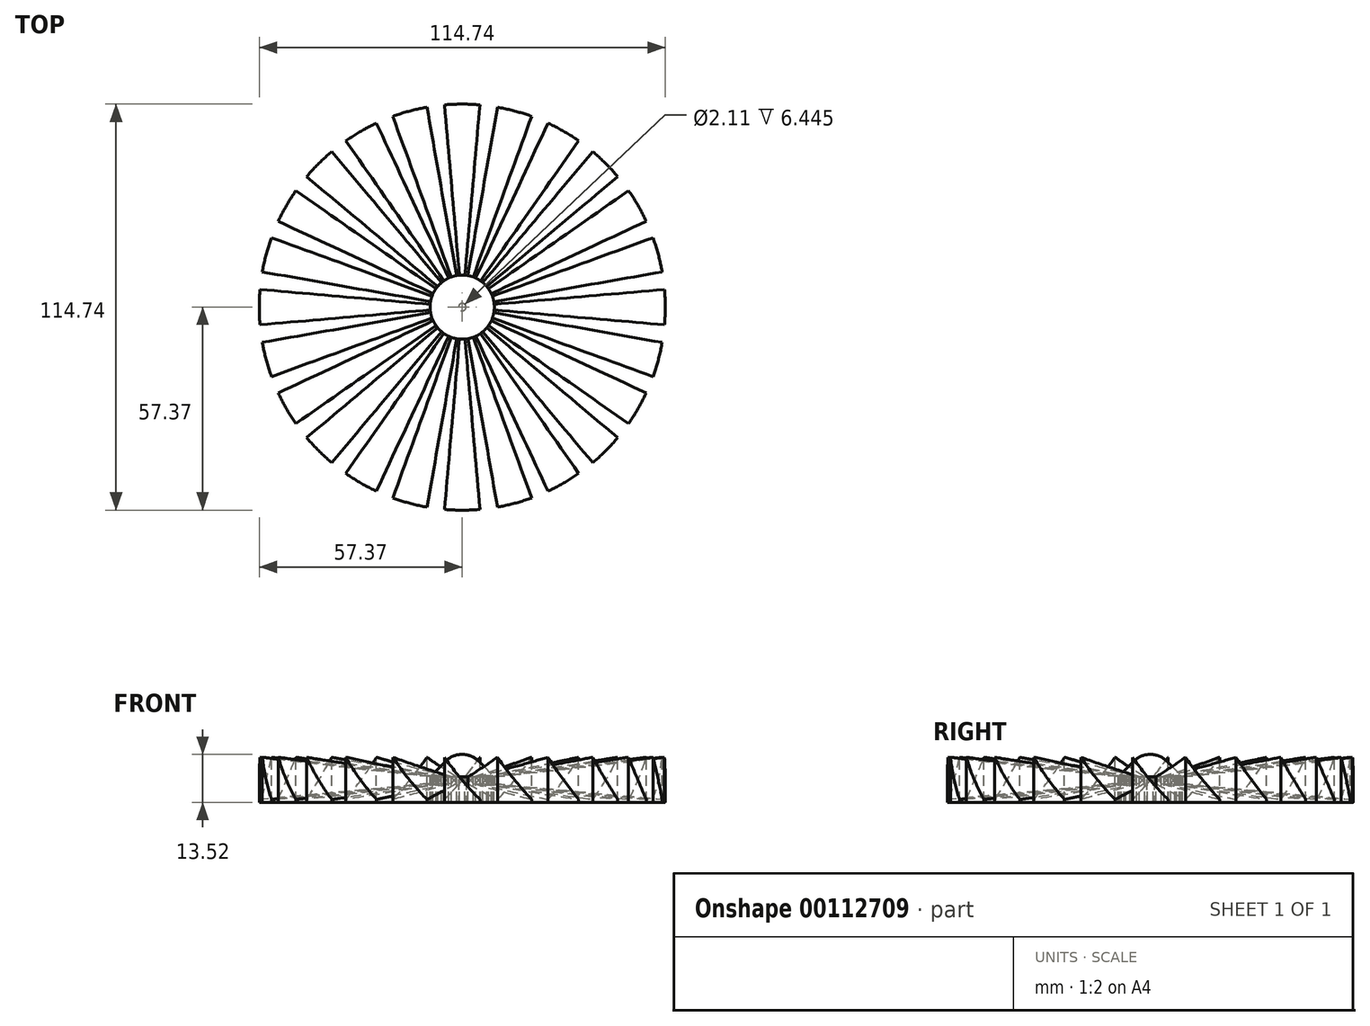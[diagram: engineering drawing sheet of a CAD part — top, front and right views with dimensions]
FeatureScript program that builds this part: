
annotation { "Feature Type Name" : "Feature", "Feature Type Description" : "" }
export const myFeature = defineFeature(function(context is Context, id is Id, definition is map)
    precondition{}
    {
        {
            var Q0;
            Q0=qCreatedBy(makeId("Top.planeOp"),FACE);
            var sketch = newSketch(context, id + "F0", { "sketchPlane" : qUnion([Q0])});
            skLineSegment(sketch, "E0", {"start": v(-5, -57.15) * mm, "end": v(5, -57.15) * mm, "construction": true});
            skLineSegment(sketch, "E1", {"start": v(0, 0) * mm, "end": v(0, -57.15) * mm, "construction": true});
            skArc(sketch, "E2", {"start": v(-5, -57.15) * mm, "mid": v(0, -57.37) * mm, "end": v(5, -57.15) * mm});
            skLineSegment(sketch, "E3", {"start": v(5, -57.15) * mm, "end": v(0.8, -9.07) * mm});
            skLineSegment(sketch, "E4", {"start": v(-5, -57.15) * mm, "end": v(-0.8, -9.07) * mm});
            skLineSegment(sketch, "E5", {"start": v(0, 0) * mm, "end": v(-0.8, -9.07) * mm});
            skLineSegment(sketch, "E6", {"start": v(0, 0) * mm, "end": v(0.8, -9.07) * mm});
            skLineSegment(sketch, "E7", {"start": v(0.8, -9.07) * mm, "end": v(-0.8, -9.07) * mm, "construction": true});
            skCircle(sketch, "E8", {"center": v(0, 0) * mm, "radius": 9.07 * mm, "construction": true});
            skSolve(sketch);
        }
        {
            var Q0;
            Q0=qSketchRegion(id+"F0",true);
            extrude(context, id + "F1", {"entities" : qUnion([Q0]), "depth" : 12.7 * mm});
        }
        {
            var Q0;
            Q0=qCreatedBy(makeId("Front.planeOp"),FACE);
            var sketch = newSketch(context, id + "F2", { "sketchPlane" : qUnion([Q0])});
            skLineSegment(sketch, "E9.bottom", {"start": v(5, 0) * mm, "end": v(-5, 0) * mm, "construction": true});
            skLineSegment(sketch, "E9.top", {"start": v(5, 12.7) * mm, "end": v(-5, 12.7) * mm});
            skLineSegment(sketch, "E9.left", {"start": v(-5, 0) * mm, "end": v(-5, 12.7) * mm, "construction": true});
            skLineSegment(sketch, "E9.right", {"start": v(5, 0.8) * mm, "end": v(5, 12.7) * mm});
            skLineSegment(sketch, "E10", {"start": v(5, 0) * mm, "end": v(5, 0.8) * mm});
            skArc(sketch, "E11", {"start": v(-5, 12.7) * mm, "mid": v(-0.26, 6.53) * mm, "end": v(5, 0.8) * mm});
            skLineSegment(sketch, "E12", {"start": v(5, 0.8) * mm, "end": v(11.73, -5.93) * mm, "construction": true});
            skSolve(sketch);
        }
        {
            var Q0;
            Q0=qSketchRegion(id+"F2",true);
            var Q1;
            Q1=makeQuery(id+"F1.opExtrude","SWEPT_FACE",FACE,{"disambiguationData":[OSD([sQuery(id+"F0.wireOp",EDGE,"E2")])]});
            extrude(context, id + "F3", {"entities" : qUnion([Q0]), "operationType" : NewBodyOperationType.REMOVE, "endBound" : BoundingType.UP_TO_SURFACE, "endBoundEntityFace" : qUnion([Q1]), "depth" : 25.4 * mm});
        }
        {
            var Q0;
            Q0=makeQuery(id+"F1.opExtrude","CAP_FACE",FACE,{"disambiguationData":[OSD([sQuery(id+"F0.wireOp",EDGE,"E2"),sQuery(id+"F0.wireOp",EDGE,"E3"),sQuery(id+"F0.wireOp",EDGE,"E4"),sQuery(id+"F0.wireOp",EDGE,"E5"),sQuery(id+"F0.wireOp",EDGE,"E6")])],"isStart":true});
            var sketch = newSketch(context, id + "F4", { "sketchPlane" : qUnion([Q0])});
            skLineSegment(sketch, "E13", {"start": v(-5, 57.15) * mm, "end": v(-5, 57.15) * mm});
            skLineSegment(sketch, "E14", {"start": v(-5, 57.15) * mm, "end": v(0, 0) * mm});
            skLineSegment(sketch, "E15", {"start": v(0, 0) * mm, "end": v(5, 57.15) * mm});
            skLineSegment(sketch, "E16", {"start": v(5, 57.15) * mm, "end": v(5, 57.15) * mm});
            skArc(sketch, "E17", {"start": v(5, 57.15) * mm, "mid": v(0, 57.37) * mm, "end": v(-5, 57.15) * mm, "construction": true});
            skArc(sketch, "E18", {"start": v(-5, 57.15) * mm, "mid": v(0, -57.37) * mm, "end": v(5, 57.15) * mm});
            skSolve(sketch);
        }
        {
            var Q0;
            Q0=qSketchRegion(id+"F4",true);
            extrude(context, id + "F5", {"entities" : qUnion([Q0]), "operationType" : NewBodyOperationType.ADD, "oppositeDirection" : true, "depth" : 12.7 * mm});
        }
        {
            var Q0;
            Q0=makeQuery(id+"F5.opExtrude","CAP_FACE",FACE,{"disambiguationData":[OSD([sQuery(id+"F4.wireOp",EDGE,"E13"),sQuery(id+"F4.wireOp",EDGE,"E14"),sQuery(id+"F4.wireOp",EDGE,"E15"),sQuery(id+"F4.wireOp",EDGE,"E16"),sQuery(id+"F4.wireOp",EDGE,"E18")])],"isStart":false});
            var sketch = newSketch(context, id + "F6", { "sketchPlane" : qUnion([Q0])});
            skCircle(sketch, "E19", {"center": v(0, 0) * mm, "radius": 9.07 * mm});
            skSolve(sketch);
        }
        {
            var Q0;
            Q0=qSketchRegion(id+"F6",true);
            var Q1;
            Q1=makeQuery(id+"F5.boolean.opBoolean","MERGE",FACE,{"derivedFrom":[makeQuery(id+"F1.opExtrude","CAP_FACE",FACE,{"disambiguationData":[OSD([sQuery(id+"F0.wireOp",EDGE,"E2"),sQuery(id+"F0.wireOp",EDGE,"E3"),sQuery(id+"F0.wireOp",EDGE,"E4"),sQuery(id+"F0.wireOp",EDGE,"E5"),sQuery(id+"F0.wireOp",EDGE,"E6")])],"isStart":true}),makeQuery(id+"F5.opExtrude","CAP_FACE",FACE,{"disambiguationData":[OSD([sQuery(id+"F4.wireOp",EDGE,"E13"),sQuery(id+"F4.wireOp",EDGE,"E14"),sQuery(id+"F4.wireOp",EDGE,"E15"),sQuery(id+"F4.wireOp",EDGE,"E16"),sQuery(id+"F4.wireOp",EDGE,"E18")])],"isStart":true})]});
            extrude(context, id + "F7", {"entities" : qUnion([Q0]), "operationType" : NewBodyOperationType.ADD, "endBound" : BoundingType.UP_TO_SURFACE, "oppositeDirection" : true, "endBoundEntityFace" : qUnion([Q1]), "depth" : 25.4 * mm});
        }
        {
            var Q0;
            Q0=makeQuery(id+"F7.opExtrude","SWEPT_FACE",FACE,{"disambiguationData":[OSD([sQuery(id+"F6.wireOp",EDGE,"E19")])]});
            var Q1;
            Q1=makeQuery(id+"F3.boolean.opBoolean","COPY",FACE,{"derivedFrom":makeQuery(id+"F3.opExtrude","SWEPT_FACE",FACE,{"disambiguationData":[OSD([sQuery(id+"F2.wireOp",EDGE,"E11")])]})});
            var Q2;
            Q2=makeQuery(id+"F5.opExtrude","SWEPT_FACE",FACE,{"disambiguationData":[OSD([sQuery(id+"F4.wireOp",EDGE,"E15")])]});
            var Q3;
            Q3=makeQuery(id+"F5.opExtrude","SWEPT_FACE",FACE,{"disambiguationData":[OSD([sQuery(id+"F4.wireOp",EDGE,"E14")])]});
            var Q4;
            Q4=makeQuery(id+"F5.boolean.opBoolean","MERGE",FACE,{"derivedFrom":[makeQuery(id+"F1.opExtrude","SWEPT_FACE",FACE,{"disambiguationData":[OSD([sQuery(id+"F0.wireOp",EDGE,"E2")])]}),makeQuery(id+"F5.opExtrude","SWEPT_FACE",FACE,{"disambiguationData":[OSD([sQuery(id+"F4.wireOp",EDGE,"E18")])]})]});
            circularPattern(context, id + "F8", {"patternType" : PatternType.FACE, "faces" : qUnion([Q0, Q1, Q2, Q3]), "axis" : qUnion([Q4]), "angle" : 15 * degree, "instanceCount" : 24});
        }
        {
            var Q0;
            Q0=makeQuery(id+"F7.boolean.opBoolean","MERGE",FACE,{"derivedFrom":[makeQuery(id+"F5.opExtrude","CAP_FACE",FACE,{"disambiguationData":[OSD([sQuery(id+"F4.wireOp",EDGE,"E14"),sQuery(id+"F4.wireOp",EDGE,"E15"),sQuery(id+"F4.wireOp",EDGE,"E18")])],"isStart":false}),makeQuery(id+"F7.opExtrude","CAP_FACE",FACE,{"disambiguationData":[OSD([sQuery(id+"F6.wireOp",EDGE,"E19")])],"isStart":true})]});
            var sketch = newSketch(context, id + "F9", { "sketchPlane" : qUnion([Q0])});
            skCircle(sketch, "E20", {"center": v(0, 0) * mm, "radius": 9.07 * mm});
            skSolve(sketch);
        }
        {
            var Q0;
            {var subQ1=makeQuery(id+"F8.opPattern","COPY",EDGE,{"derivedFrom":makeQuery(id+"F5.opExtrude","CAP_EDGE",EDGE,{"disambiguationData":[OSD([sQuery(id+"F4.wireOp",EDGE,"E14")])],"isStart":false}),"instanceName":"2"});Q0=makeQuery(id+"F9.imprint","IMPRINT",FACE,{"disambiguationData":[TD([[makeQuery(id+"F9.imprint","IMPRINT",EDGE,{"derivedFrom":subQ1}),1.0]])]});}
            var Q1;
            {var subQ1=makeQuery(id+"F8.opPattern","COPY",EDGE,{"derivedFrom":makeQuery(id+"F5.opExtrude","CAP_EDGE",EDGE,{"disambiguationData":[OSD([sQuery(id+"F4.wireOp",EDGE,"E14")])],"isStart":false}),"instanceName":"1"});Q1=makeQuery(id+"F9.imprint","IMPRINT",FACE,{"disambiguationData":[TD([[makeQuery(id+"F9.imprint","IMPRINT",EDGE,{"derivedFrom":subQ1}),1.0]])]});}
            var Q2;
            {var subQ1=makeQuery(id+"F5.opExtrude","CAP_EDGE",EDGE,{"disambiguationData":[OSD([sQuery(id+"F4.wireOp",EDGE,"E14")])],"isStart":false});Q2=makeQuery(id+"F9.imprint","IMPRINT",FACE,{"disambiguationData":[TD([[makeQuery(id+"F9.imprint","IMPRINT",EDGE,{"derivedFrom":subQ1}),1.0]])]});}
            var Q3;
            {var subQ1=makeQuery(id+"F5.opExtrude","CAP_EDGE",EDGE,{"disambiguationData":[OSD([sQuery(id+"F4.wireOp",EDGE,"E15")])],"isStart":false});Q3=makeQuery(id+"F9.imprint","IMPRINT",FACE,{"disambiguationData":[TD([[makeQuery(id+"F9.imprint","IMPRINT",EDGE,{"derivedFrom":subQ1}),-1.0]])]});}
            var Q4;
            {var subQ1=makeQuery(id+"F8.opPattern","COPY",EDGE,{"derivedFrom":makeQuery(id+"F5.opExtrude","CAP_EDGE",EDGE,{"disambiguationData":[OSD([sQuery(id+"F4.wireOp",EDGE,"E14")])],"isStart":false}),"instanceName":"8"});Q4=makeQuery(id+"F9.imprint","IMPRINT",FACE,{"disambiguationData":[TD([[makeQuery(id+"F9.imprint","IMPRINT",EDGE,{"derivedFrom":subQ1}),1.0]])]});}
            var Q5;
            {var subQ1=makeQuery(id+"F8.opPattern","COPY",EDGE,{"derivedFrom":makeQuery(id+"F5.opExtrude","CAP_EDGE",EDGE,{"disambiguationData":[OSD([sQuery(id+"F4.wireOp",EDGE,"E14")])],"isStart":false}),"instanceName":"7"});Q5=makeQuery(id+"F9.imprint","IMPRINT",FACE,{"disambiguationData":[TD([[makeQuery(id+"F9.imprint","IMPRINT",EDGE,{"derivedFrom":subQ1}),1.0]])]});}
            var Q6;
            {var subQ1=makeQuery(id+"F8.opPattern","COPY",EDGE,{"derivedFrom":makeQuery(id+"F5.opExtrude","CAP_EDGE",EDGE,{"disambiguationData":[OSD([sQuery(id+"F4.wireOp",EDGE,"E14")])],"isStart":false}),"instanceName":"6"});Q6=makeQuery(id+"F9.imprint","IMPRINT",FACE,{"disambiguationData":[TD([[makeQuery(id+"F9.imprint","IMPRINT",EDGE,{"derivedFrom":subQ1}),1.0]])]});}
            var Q7;
            {var subQ1=makeQuery(id+"F8.opPattern","COPY",EDGE,{"derivedFrom":makeQuery(id+"F5.opExtrude","CAP_EDGE",EDGE,{"disambiguationData":[OSD([sQuery(id+"F4.wireOp",EDGE,"E14")])],"isStart":false}),"instanceName":"5"});Q7=makeQuery(id+"F9.imprint","IMPRINT",FACE,{"disambiguationData":[TD([[makeQuery(id+"F9.imprint","IMPRINT",EDGE,{"derivedFrom":subQ1}),1.0]])]});}
            var Q8;
            {var subQ1=makeQuery(id+"F8.opPattern","COPY",EDGE,{"derivedFrom":makeQuery(id+"F5.opExtrude","CAP_EDGE",EDGE,{"disambiguationData":[OSD([sQuery(id+"F4.wireOp",EDGE,"E14")])],"isStart":false}),"instanceName":"4"});Q8=makeQuery(id+"F9.imprint","IMPRINT",FACE,{"disambiguationData":[TD([[makeQuery(id+"F9.imprint","IMPRINT",EDGE,{"derivedFrom":subQ1}),1.0]])]});}
            var Q9;
            {var subQ1=makeQuery(id+"F8.opPattern","COPY",EDGE,{"derivedFrom":makeQuery(id+"F5.opExtrude","CAP_EDGE",EDGE,{"disambiguationData":[OSD([sQuery(id+"F4.wireOp",EDGE,"E14")])],"isStart":false}),"instanceName":"3"});Q9=makeQuery(id+"F9.imprint","IMPRINT",FACE,{"disambiguationData":[TD([[makeQuery(id+"F9.imprint","IMPRINT",EDGE,{"derivedFrom":subQ1}),1.0]])]});}
            var Q10;
            {var subQ1=makeQuery(id+"F8.opPattern","COPY",EDGE,{"derivedFrom":makeQuery(id+"F5.opExtrude","CAP_EDGE",EDGE,{"disambiguationData":[OSD([sQuery(id+"F4.wireOp",EDGE,"E14")])],"isStart":false}),"instanceName":"9"});Q10=makeQuery(id+"F9.imprint","IMPRINT",FACE,{"disambiguationData":[TD([[makeQuery(id+"F9.imprint","IMPRINT",EDGE,{"derivedFrom":subQ1}),1.0]])]});}
            var Q11;
            {var subQ1=makeQuery(id+"F8.opPattern","COPY",EDGE,{"derivedFrom":makeQuery(id+"F5.opExtrude","CAP_EDGE",EDGE,{"disambiguationData":[OSD([sQuery(id+"F4.wireOp",EDGE,"E14")])],"isStart":false}),"instanceName":"10"});Q11=makeQuery(id+"F9.imprint","IMPRINT",FACE,{"disambiguationData":[TD([[makeQuery(id+"F9.imprint","IMPRINT",EDGE,{"derivedFrom":subQ1}),1.0]])]});}
            var Q12;
            {var subQ1=makeQuery(id+"F8.opPattern","COPY",EDGE,{"derivedFrom":makeQuery(id+"F5.opExtrude","CAP_EDGE",EDGE,{"disambiguationData":[OSD([sQuery(id+"F4.wireOp",EDGE,"E14")])],"isStart":false}),"instanceName":"11"});Q12=makeQuery(id+"F9.imprint","IMPRINT",FACE,{"disambiguationData":[TD([[makeQuery(id+"F9.imprint","IMPRINT",EDGE,{"derivedFrom":subQ1}),1.0]])]});}
            var Q13;
            {var subQ1=makeQuery(id+"F8.opPattern","COPY",EDGE,{"derivedFrom":makeQuery(id+"F5.opExtrude","CAP_EDGE",EDGE,{"disambiguationData":[OSD([sQuery(id+"F4.wireOp",EDGE,"E14")])],"isStart":false}),"instanceName":"12"});Q13=makeQuery(id+"F9.imprint","IMPRINT",FACE,{"disambiguationData":[TD([[makeQuery(id+"F9.imprint","IMPRINT",EDGE,{"derivedFrom":subQ1}),1.0]])]});}
            var Q14;
            {var subQ1=makeQuery(id+"F8.opPattern","COPY",EDGE,{"derivedFrom":makeQuery(id+"F5.opExtrude","CAP_EDGE",EDGE,{"disambiguationData":[OSD([sQuery(id+"F4.wireOp",EDGE,"E14")])],"isStart":false}),"instanceName":"13"});Q14=makeQuery(id+"F9.imprint","IMPRINT",FACE,{"disambiguationData":[TD([[makeQuery(id+"F9.imprint","IMPRINT",EDGE,{"derivedFrom":subQ1}),1.0]])]});}
            var Q15;
            {var subQ1=makeQuery(id+"F8.opPattern","COPY",EDGE,{"derivedFrom":makeQuery(id+"F5.opExtrude","CAP_EDGE",EDGE,{"disambiguationData":[OSD([sQuery(id+"F4.wireOp",EDGE,"E14")])],"isStart":false}),"instanceName":"14"});Q15=makeQuery(id+"F9.imprint","IMPRINT",FACE,{"disambiguationData":[TD([[makeQuery(id+"F9.imprint","IMPRINT",EDGE,{"derivedFrom":subQ1}),1.0]])]});}
            var Q16;
            {var subQ1=makeQuery(id+"F8.opPattern","COPY",EDGE,{"derivedFrom":makeQuery(id+"F5.opExtrude","CAP_EDGE",EDGE,{"disambiguationData":[OSD([sQuery(id+"F4.wireOp",EDGE,"E14")])],"isStart":false}),"instanceName":"15"});Q16=makeQuery(id+"F9.imprint","IMPRINT",FACE,{"disambiguationData":[TD([[makeQuery(id+"F9.imprint","IMPRINT",EDGE,{"derivedFrom":subQ1}),1.0]])]});}
            var Q17;
            {var subQ1=makeQuery(id+"F8.opPattern","COPY",EDGE,{"derivedFrom":makeQuery(id+"F5.opExtrude","CAP_EDGE",EDGE,{"disambiguationData":[OSD([sQuery(id+"F4.wireOp",EDGE,"E14")])],"isStart":false}),"instanceName":"16"});Q17=makeQuery(id+"F9.imprint","IMPRINT",FACE,{"disambiguationData":[TD([[makeQuery(id+"F9.imprint","IMPRINT",EDGE,{"derivedFrom":subQ1}),1.0]])]});}
            var Q18;
            {var subQ1=makeQuery(id+"F8.opPattern","COPY",EDGE,{"derivedFrom":makeQuery(id+"F5.opExtrude","CAP_EDGE",EDGE,{"disambiguationData":[OSD([sQuery(id+"F4.wireOp",EDGE,"E14")])],"isStart":false}),"instanceName":"17"});Q18=makeQuery(id+"F9.imprint","IMPRINT",FACE,{"disambiguationData":[TD([[makeQuery(id+"F9.imprint","IMPRINT",EDGE,{"derivedFrom":subQ1}),1.0]])]});}
            var Q19;
            {var subQ1=makeQuery(id+"F8.opPattern","COPY",EDGE,{"derivedFrom":makeQuery(id+"F5.opExtrude","CAP_EDGE",EDGE,{"disambiguationData":[OSD([sQuery(id+"F4.wireOp",EDGE,"E14")])],"isStart":false}),"instanceName":"18"});Q19=makeQuery(id+"F9.imprint","IMPRINT",FACE,{"disambiguationData":[TD([[makeQuery(id+"F9.imprint","IMPRINT",EDGE,{"derivedFrom":subQ1}),1.0]])]});}
            var Q20;
            {var subQ1=makeQuery(id+"F8.opPattern","COPY",EDGE,{"derivedFrom":makeQuery(id+"F5.opExtrude","CAP_EDGE",EDGE,{"disambiguationData":[OSD([sQuery(id+"F4.wireOp",EDGE,"E14")])],"isStart":false}),"instanceName":"19"});Q20=makeQuery(id+"F9.imprint","IMPRINT",FACE,{"disambiguationData":[TD([[makeQuery(id+"F9.imprint","IMPRINT",EDGE,{"derivedFrom":subQ1}),1.0]])]});}
            var Q21;
            {var subQ1=makeQuery(id+"F8.opPattern","COPY",EDGE,{"derivedFrom":makeQuery(id+"F5.opExtrude","CAP_EDGE",EDGE,{"disambiguationData":[OSD([sQuery(id+"F4.wireOp",EDGE,"E14")])],"isStart":false}),"instanceName":"20"});Q21=makeQuery(id+"F9.imprint","IMPRINT",FACE,{"disambiguationData":[TD([[makeQuery(id+"F9.imprint","IMPRINT",EDGE,{"derivedFrom":subQ1}),1.0]])]});}
            var Q22;
            {var subQ1=makeQuery(id+"F8.opPattern","COPY",EDGE,{"derivedFrom":makeQuery(id+"F5.opExtrude","CAP_EDGE",EDGE,{"disambiguationData":[OSD([sQuery(id+"F4.wireOp",EDGE,"E14")])],"isStart":false}),"instanceName":"21"});Q22=makeQuery(id+"F9.imprint","IMPRINT",FACE,{"disambiguationData":[TD([[makeQuery(id+"F9.imprint","IMPRINT",EDGE,{"derivedFrom":subQ1}),1.0]])]});}
            var Q23;
            {var subQ1=makeQuery(id+"F8.opPattern","COPY",EDGE,{"derivedFrom":makeQuery(id+"F5.opExtrude","CAP_EDGE",EDGE,{"disambiguationData":[OSD([sQuery(id+"F4.wireOp",EDGE,"E14")])],"isStart":false}),"instanceName":"22"});Q23=makeQuery(id+"F9.imprint","IMPRINT",FACE,{"disambiguationData":[TD([[makeQuery(id+"F9.imprint","IMPRINT",EDGE,{"derivedFrom":subQ1}),1.0]])]});}
            var Q24;
            Q24=makeQuery(id+"F5.boolean.opBoolean","MERGE",FACE,{"derivedFrom":[makeQuery(id+"F1.opExtrude","CAP_FACE",FACE,{"disambiguationData":[OSD([sQuery(id+"F0.wireOp",EDGE,"E2"),sQuery(id+"F0.wireOp",EDGE,"E3"),sQuery(id+"F0.wireOp",EDGE,"E4"),sQuery(id+"F0.wireOp",EDGE,"E5"),sQuery(id+"F0.wireOp",EDGE,"E6")])],"isStart":true}),makeQuery(id+"F5.opExtrude","CAP_FACE",FACE,{"disambiguationData":[OSD([sQuery(id+"F4.wireOp",EDGE,"E14"),sQuery(id+"F4.wireOp",EDGE,"E15"),sQuery(id+"F4.wireOp",EDGE,"E18")])],"isStart":true})]});
            extrude(context, id + "F10", {"entities" : qUnion([Q0, Q1, Q2, Q3, Q4, Q5, Q6, Q7, Q8, Q9, Q10, Q11, Q12, Q13, Q14, Q15, Q16, Q17, Q18, Q19, Q20, Q21, Q22, Q23]), "operationType" : NewBodyOperationType.REMOVE, "endBound" : BoundingType.UP_TO_SURFACE, "oppositeDirection" : true, "endBoundEntityFace" : qUnion([Q24]), "depth" : 25.4 * mm});
        }
        {
            var Q0;
            Q0=makeQuery(id+"F5.boolean.opBoolean","MERGE",FACE,{"derivedFrom":[makeQuery(id+"F1.opExtrude","CAP_FACE",FACE,{"disambiguationData":[OSD([sQuery(id+"F0.wireOp",EDGE,"E2"),sQuery(id+"F0.wireOp",EDGE,"E3"),sQuery(id+"F0.wireOp",EDGE,"E4"),sQuery(id+"F0.wireOp",EDGE,"E5"),sQuery(id+"F0.wireOp",EDGE,"E6")])],"isStart":true}),makeQuery(id+"F5.opExtrude","CAP_FACE",FACE,{"disambiguationData":[OSD([sQuery(id+"F4.wireOp",EDGE,"E14"),sQuery(id+"F4.wireOp",EDGE,"E15"),sQuery(id+"F4.wireOp",EDGE,"E18")])],"isStart":true})]});
            var sketch = newSketch(context, id + "F11", { "sketchPlane" : qUnion([Q0])});
            skCircle(sketch, "E21", {"center": v(0, 0) * mm, "radius": 1.05 * mm});
            skSolve(sketch);
        }
        {
            var Q0;
            Q0=qSketchRegion(id+"F11",true);
            extrude(context, id + "F12", {"entities" : qUnion([Q0]), "operationType" : NewBodyOperationType.REMOVE, "oppositeDirection" : true, "depth" : 6.45 * mm});
        }
        {
            var Q0;
            Q0=makeQuery(id+"F7.boolean.opBoolean","MERGE",FACE,{"derivedFrom":[makeQuery(id+"F5.opExtrude","CAP_FACE",FACE,{"disambiguationData":[OSD([sQuery(id+"F4.wireOp",EDGE,"E14"),sQuery(id+"F4.wireOp",EDGE,"E15"),sQuery(id+"F4.wireOp",EDGE,"E18")])],"isStart":false}),makeQuery(id+"F7.opExtrude","CAP_FACE",FACE,{"disambiguationData":[OSD([sQuery(id+"F6.wireOp",EDGE,"E19")])],"isStart":true})]});
            extrude(context, id + "F13", {"entities" : qUnion([Q0]), "operationType" : NewBodyOperationType.ADD, "depth" : 0.82 * mm});
        }
        {
            var Q0;
            Q0=qCreatedBy(makeId("Front.planeOp"),FACE);
            var sketch = newSketch(context, id + "F14", { "sketchPlane" : qUnion([Q0])});
            skLineSegment(sketch, "E22.top", {"start": v(0, 22.6) * mm, "end": v(-9.07, 22.6) * mm});
            skLineSegment(sketch, "E22.left", {"start": v(0, 13.52) * mm, "end": v(0, 22.6) * mm});
            skLineSegment(sketch, "E22.right", {"start": v(-9.07, 7.17) * mm, "end": v(-9.07, 22.6) * mm});
            skLineSegment(sketch, "E23", {"start": v(0, 13.52) * mm, "end": v(0, 7.17) * mm, "construction": true});
            skLineSegment(sketch, "E24", {"start": v(0, 7.17) * mm, "end": v(-9.07, 7.17) * mm, "construction": true});
            skArc(sketch, "E25", {"start": v(0, 13.52) * mm, "mid": v(-2.52, 13.02) * mm, "end": v(-4.65, 11.6) * mm});
            skLineSegment(sketch, "E26", {"start": v(-4.65, 11.6) * mm, "end": v(-9.07, 7.17) * mm});
            skSolve(sketch);
        }
        {
            var Q0;
            Q0=qSketchRegion(id+"F14",true);
            var Q1;
            Q1=makeQuery(id+"F13.opExtrude","CAP_EDGE",EDGE,{"disambiguationData":[OSD([sQuery(id+"F6.wireOp",EDGE,"E19"),sQuery(id+"F9.wireOp",EDGE,"E20")])],"isStart":false});
            revolve(context, id + "F15", {"operationType" : NewBodyOperationType.REMOVE, "entities" : qUnion([Q0]), "axis" : qUnion([Q1]), "revolveType" : RevolveType.FULL, "oppositeDirection" : true});
        }
    });
